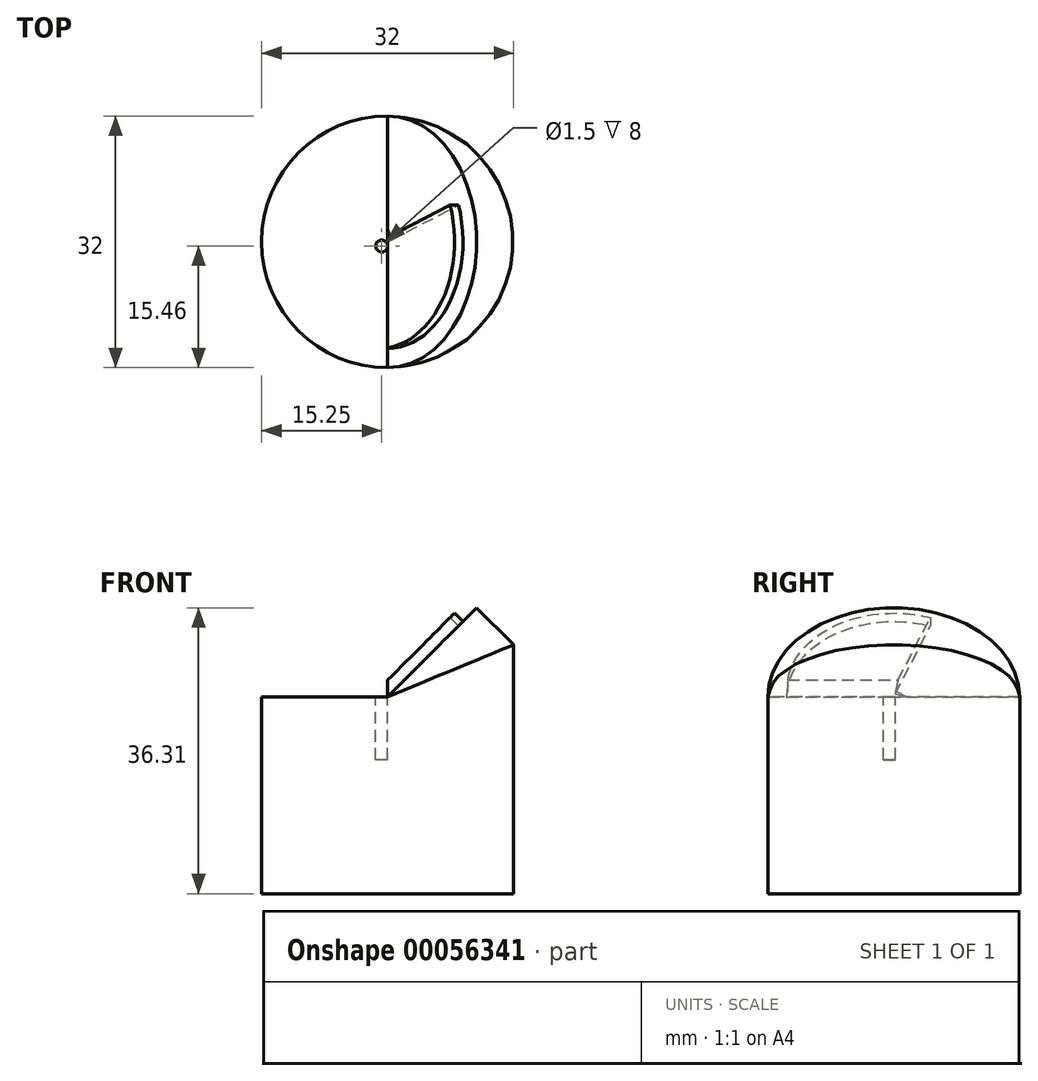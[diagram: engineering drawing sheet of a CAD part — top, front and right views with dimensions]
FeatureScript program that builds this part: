
annotation { "Feature Type Name" : "Feature", "Feature Type Description" : "" }
export const myFeature = defineFeature(function(context is Context, id is Id, definition is map)
    precondition{}
    {
        {
            var Q0;
            Q0=qCreatedBy(makeId("Top.planeOp"),FACE);
            var sketch = newSketch(context, id + "F0", { "sketchPlane" : qUnion([Q0])});
            skCircle(sketch, "E0", {"center": v(0, 0) * mm, "radius": 16 * mm});
            skLineSegment(sketch, "E1", {"start": v(0, 0) * mm, "end": v(0, -16) * mm, "construction": true});
            skSolve(sketch);
        }
        {
            var Q0;
            Q0=qCreatedBy(makeId("Front.planeOp"),FACE);
            var sketch = newSketch(context, id + "F1", { "sketchPlane" : qUnion([Q0])});
            skLineSegment(sketch, "E2", {"start": v(0, 0) * mm, "end": v(16, 0) * mm});
            skLineSegment(sketch, "E3", {"start": v(16, 0) * mm, "end": v(16, 16) * mm});
            skLineSegment(sketch, "E4", {"start": v(0, 0) * mm, "end": v(16, 16) * mm});
            skSolve(sketch);
        }
        {
            var Q0;
            Q0=makeQuery(id+"F1.imprint","IMPRINT",FACE,{"disambiguationData":[TD([[makeQuery(id+"F1.imprint","IMPRINT",EDGE,{"derivedFrom":sQuery(id+"F1.wireOp",EDGE,"E2")}),1.0]])]});
            extrude(context, id + "F2", {"entities" : qUnion([Q0]), "endBound" : BoundingType.SYMMETRIC, "depth" : 32 * mm});
        }
        {
            var Q0;
            Q0=makeQuery(id+"F0.imprint","IMPRINT",FACE,{"disambiguationData":[TD([[makeQuery(id+"F0.imprint","IMPRINT",EDGE,{"derivedFrom":sQuery(id+"F0.wireOp",EDGE,"E0")}),1.0]])]});
            extrude(context, id + "F3", {"entities" : qUnion([Q0]), "operationType" : NewBodyOperationType.INTERSECT, "depth" : 25 * mm});
        }
        {
            var Q0;
            Q0=makeQuery(id+"F0.imprint","IMPRINT",FACE,{"disambiguationData":[TD([[makeQuery(id+"F0.imprint","IMPRINT",EDGE,{"derivedFrom":sQuery(id+"F0.wireOp",EDGE,"E0")}),1.0]])]});
            extrude(context, id + "F4", {"entities" : qUnion([Q0]), "operationType" : NewBodyOperationType.ADD, "oppositeDirection" : true, "depth" : 25 * mm});
        }
        {
            var Q0;
            Q0=makeQuery(id+"F2.opExtrude","SWEPT_FACE",FACE,{"disambiguationData":[OSD([sQuery(id+"F1.wireOp",EDGE,"E4")])]});
            var sketch = newSketch(context, id + "F5", { "sketchPlane" : qUnion([Q0])});
            skLineSegment(sketch, "E5", {"start": v(0, 0) * mm, "end": v(0.54, 0) * mm});
            skLineSegment(sketch, "E6", {"start": v(0.54, 0) * mm, "end": v(13.54, 0) * mm});
            skArc(sketch, "E7", {"start": v(13.54, 0) * mm, "mid": v(7.76, 11.1) * mm, "end": v(-4.64, 12.72) * mm});
            skLineSegment(sketch, "E8", {"start": v(0, 0) * mm, "end": v(-4.64, 12.72) * mm});
            skLineSegment(sketch, "E9", {"start": v(-4.64, 12.72) * mm, "end": v(-0.18, 0.5) * mm});
            skSolve(sketch);
        }
        {
            var Q0;
            Q0=makeQuery(id+"F5.imprint","IMPRINT",FACE,{"disambiguationData":[TD([[makeQuery(id+"F5.imprint","IMPRINT",EDGE,{"derivedFrom":sQuery(id+"F5.wireOp",EDGE,"E5")}),-1.0]])]});
            var Q1;
            Q1=sQuery(id+"F5.wireOp",EDGE,"E7");
            extrude(context, id + "F6", {"entities" : qUnion([Q0]), "operationType" : NewBodyOperationType.ADD, "surfaceEntities" : qUnion([Q1]), "depth" : 1.5 * mm});
        }
        {
            var Q0;
            {var subQ3=sQuery(id+"F5.wireOp",EDGE,"E7");Q0=makeQuery(id+"F5.imprint","IMPRINT",FACE,{"disambiguationData":[TD([[makeQuery(id+"F5.imprint","IMPRINT",EDGE,{"derivedFrom":subQ3}),-1.0]])]});}
            var sketch = newSketch(context, id + "F7", { "sketchPlane" : qUnion([Q0])});
            skLineSegment(sketch, "E10", {"start": v(-0.18, 0.5) * mm, "end": v(-1.58, 0) * mm});
            skLineSegment(sketch, "E11", {"start": v(-1.58, 0) * mm, "end": v(0, 0) * mm});
            skLineSegment(sketch, "E12", {"start": v(0, 0) * mm, "end": v(-0.18, 0.5) * mm});
            skSolve(sketch);
        }
        {
            var Q0;
            Q0 = qSketchRegion(id + "F7", true);
            extrude(context, id + "F8", {"entities" : qUnion([Q0]), "operationType" : NewBodyOperationType.ADD, "depth" : 10 * mm});
        }
        {
            var Q0;
            Q0=makeQuery(id+"F0.imprint","IMPRINT",FACE,{"disambiguationData":[TD([[makeQuery(id+"F0.imprint","IMPRINT",EDGE,{"derivedFrom":sQuery(id+"F0.wireOp",EDGE,"E0")}),1.0]])]});
            var sketch = newSketch(context, id + "F9", { "sketchPlane" : qUnion([Q0])});
            skArc(sketch, "E13", {"start": v(0, -16) * mm, "mid": v(-16, 0) * mm, "end": v(0, 16) * mm});
            skLineSegment(sketch, "E14", {"start": v(0, 16) * mm, "end": v(0, -16) * mm});
            skSolve(sketch);
        }
        {
            var Q0;
            Q0=makeQuery(id+"F9.imprint","IMPRINT",FACE,{"disambiguationData":[TD([[makeQuery(id+"F9.imprint","IMPRINT",EDGE,{"derivedFrom":sQuery(id+"F9.wireOp",EDGE,"E13")}),1.0]])]});
            extrude(context, id + "F10", {"entities" : qUnion([Q0]), "operationType" : NewBodyOperationType.REMOVE, "depth" : 25 * mm});
        }
        {
            var Q0;
            Q0=makeQuery(id+"F0.imprint","IMPRINT",FACE,{"disambiguationData":[TD([[makeQuery(id+"F0.imprint","IMPRINT",EDGE,{"derivedFrom":sQuery(id+"F0.wireOp",EDGE,"E0")}),1.0]])]});
            var sketch = newSketch(context, id + "F11", { "sketchPlane" : qUnion([Q0])});
            skLineSegment(sketch, "E15", {"start": v(0, -0.54) * mm, "end": v(-0.75, -0.54) * mm, "construction": true});
            skCircle(sketch, "E16", {"center": v(-0.75, -0.54) * mm, "radius": 0.75 * mm});
            skSolve(sketch);
        }
        {
            var Q0;
            Q0=makeQuery(id+"F11.imprint","IMPRINT",FACE,{"disambiguationData":[TD([[makeQuery(id+"F11.imprint","IMPRINT",EDGE,{"derivedFrom":sQuery(id+"F11.wireOp",EDGE,"E16")}),1.0]])]});
            extrude(context, id + "F12", {"entities" : qUnion([Q0]), "operationType" : NewBodyOperationType.REMOVE, "oppositeDirection" : true, "depth" : 8 * mm});
        }
        {
            var Q0;
            {var subQ3=sQuery(id+"F5.wireOp",EDGE,"E7");Q0=makeQuery(id+"F5.imprint","IMPRINT",FACE,{"disambiguationData":[TD([[makeQuery(id+"F5.imprint","IMPRINT",EDGE,{"derivedFrom":subQ3}),-1.0]])]});}
            var sketch = newSketch(context, id + "F13", { "sketchPlane" : qUnion([Q0])});
            skArc(sketch, "E17", {"start": v(16, 0) * mm, "mid": v(0, 16) * mm, "end": v(-16, 0) * mm});
            skSolve(sketch);
        }
        {
            var Q0;
            Q0=makeQuery(id+"F13.imprint","IMPRINT",FACE,{"disambiguationData":[TD([[makeQuery(id+"F13.imprint","IMPRINT",EDGE,{"derivedFrom":sQuery(id+"F13.wireOp",EDGE,"E17")}),-1.0]])]});
            extrude(context, id + "F14", {"entities" : qUnion([Q0]), "operationType" : NewBodyOperationType.REMOVE, "oppositeDirection" : true, "depth" : 25 * mm});
        }
    });
